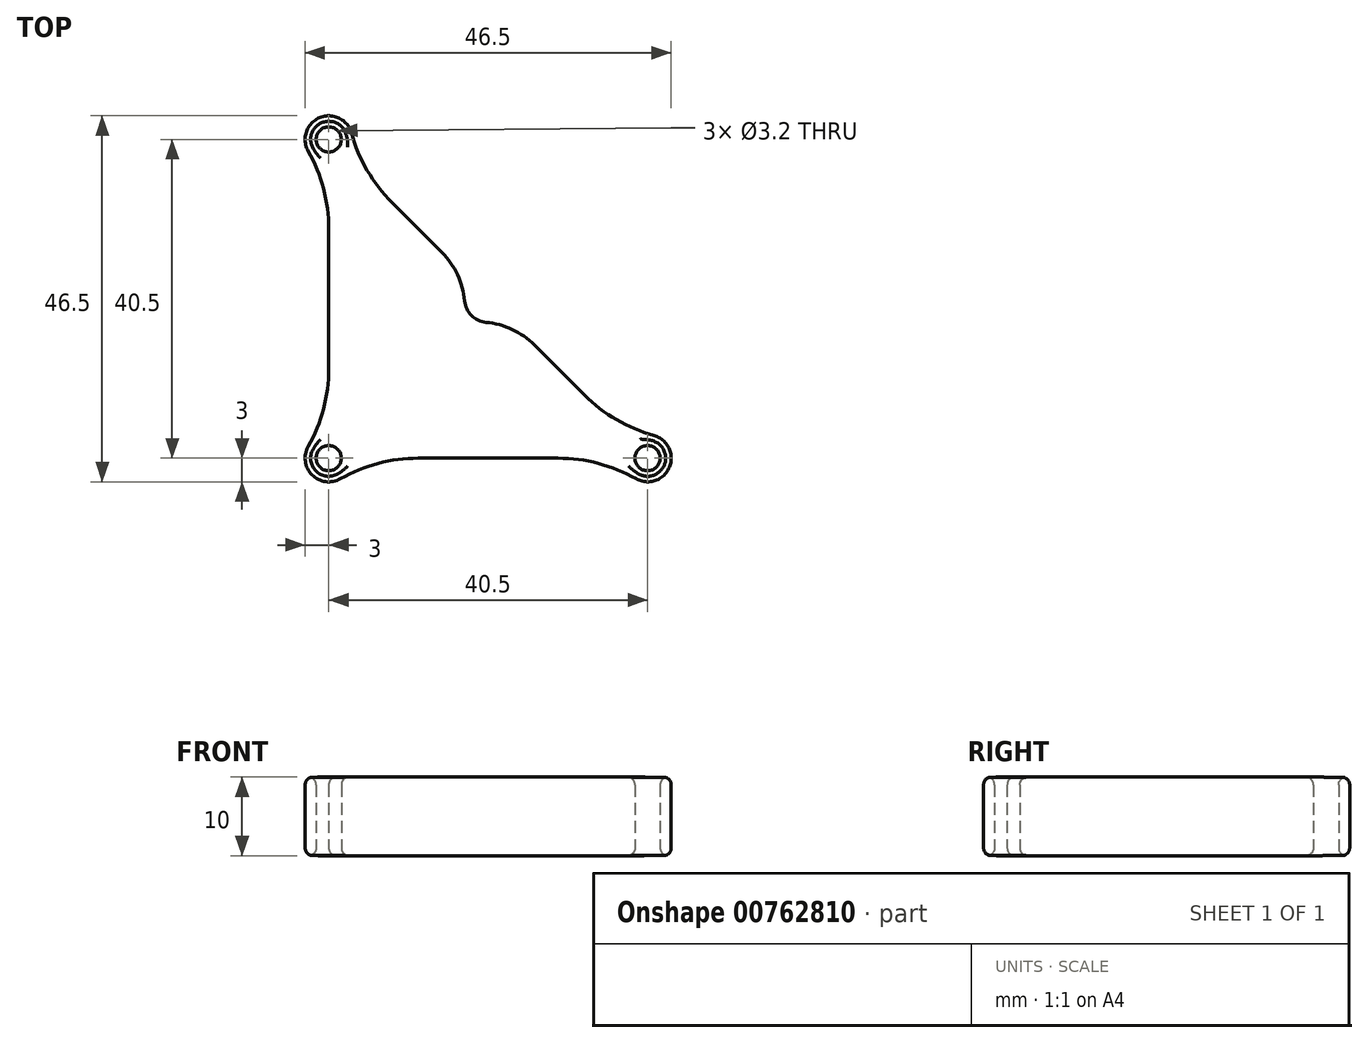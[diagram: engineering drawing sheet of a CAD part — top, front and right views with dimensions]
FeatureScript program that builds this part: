
annotation { "Feature Type Name" : "Feature", "Feature Type Description" : "" }
export const myFeature = defineFeature(function(context is Context, id is Id, definition is map)
    precondition{}
    {
        {
            var Q0;
            Q0=qCreatedBy(makeId("Top.planeOp"),FACE);
            var sketch = newSketch(context, id + "F0", { "sketchPlane" : qUnion([Q0])});
            skLineSegment(sketch, "E0", {"start": v(29.14, 0) * mm, "end": v(11.36, 0) * mm});
            skLineSegment(sketch, "E1", {"start": v(0, 11.36) * mm, "end": v(0, 29.14) * mm});
            skLineSegment(sketch, "E2", {"start": v(8.03, 32.47) * mm, "end": v(14.38, 26.12) * mm});
            skArc(sketch, "E3", {"start": v(17.26, 19.97) * mm, "mid": v(18.13, 18.13) * mm, "end": v(19.97, 17.26) * mm});
            skArc(sketch, "E4", {"start": v(2.9, 41.3) * mm, "mid": v(-1.15, 43.27) * mm, "end": v(-2.6, 39.02) * mm});
            skArc(sketch, "E5", {"start": v(-2.6, 1.48) * mm, "mid": v(-2.12, -2.12) * mm, "end": v(1.48, -2.6) * mm});
            skArc(sketch, "E6", {"start": v(39.02, -2.6) * mm, "mid": v(43.27, -1.15) * mm, "end": v(41.3, 2.9) * mm});
            skLineSegment(sketch, "E7.trimOffspring", {"start": v(26.12, 14.38) * mm, "end": v(32.47, 8.03) * mm});
            skPoint(sketch, "E8.visualSharp", {"position": v(2.12, 38.38) * mm});
            skArc(sketch, "E8.filletArc", {"start": v(2.9, 41.3) * mm, "mid": v(4.89, 36.55) * mm, "end": v(8.03, 32.47) * mm});
            skPoint(sketch, "E9.visualSharp", {"position": v(0, 37.5) * mm});
            skArc(sketch, "E9.filletArc", {"start": v(0, 29.14) * mm, "mid": v(-0.66, 34.25) * mm, "end": v(-2.6, 39.02) * mm});
            skPoint(sketch, "E10.visualSharp", {"position": v(0, 3) * mm});
            skArc(sketch, "E10.filletArc", {"start": v(-2.6, 1.48) * mm, "mid": v(-0.66, 6.25) * mm, "end": v(0, 11.36) * mm});
            skPoint(sketch, "E11.visualSharp", {"position": v(3, 0) * mm});
            skArc(sketch, "E11.filletArc", {"start": v(11.36, 0) * mm, "mid": v(6.25, -0.66) * mm, "end": v(1.48, -2.6) * mm});
            skPoint(sketch, "E12.visualSharp", {"position": v(37.5, 0) * mm});
            skArc(sketch, "E12.filletArc", {"start": v(39.02, -2.6) * mm, "mid": v(34.25, -0.66) * mm, "end": v(29.14, 0) * mm});
            skPoint(sketch, "E13.visualSharp", {"position": v(38.38, 2.12) * mm});
            skArc(sketch, "E13.filletArc", {"start": v(32.47, 8.03) * mm, "mid": v(36.55, 4.89) * mm, "end": v(41.3, 2.9) * mm});
            skPoint(sketch, "E14.visualSharp", {"position": v(18.13, 22.37) * mm});
            skArc(sketch, "E14.filletArc", {"start": v(17.26, 19.97) * mm, "mid": v(16.36, 23.3) * mm, "end": v(14.38, 26.12) * mm});
            skPoint(sketch, "E15.visualSharp", {"position": v(22.37, 18.13) * mm});
            skArc(sketch, "E15.filletArc", {"start": v(26.12, 14.38) * mm, "mid": v(23.3, 16.36) * mm, "end": v(19.97, 17.26) * mm});
            skCircle(sketch, "E16", {"center": v(0, 40.5) * mm, "radius": 1.6 * mm});
            skCircle(sketch, "E17", {"center": v(0, 0) * mm, "radius": 1.6 * mm});
            skCircle(sketch, "E18", {"center": v(40.5, 0) * mm, "radius": 1.6 * mm});
            skSolve(sketch);
        }
        {
            var Q0;
            Q0=makeQuery(id+"F0.imprint","IMPRINT",FACE,{"disambiguationData":[TD([[makeQuery(id+"F0.imprint","IMPRINT",EDGE,{"derivedFrom":sQuery(id+"F0.wireOp",EDGE,"E0")}),-1.0]])]});
            extrude(context, id + "F1", {"entities" : qUnion([Q0]), "depth" : 10 * mm, "offsetDistance" : 25 * mm});
        }
        {
            var Q0;
            Q0=makeQuery(id+"F1.opExtrude","CAP_FACE",FACE,{"disambiguationData":[OSD([sQuery(id+"F0.wireOp",EDGE,"E0"),sQuery(id+"F0.wireOp",EDGE,"E1"),sQuery(id+"F0.wireOp",EDGE,"E2"),sQuery(id+"F0.wireOp",EDGE,"E3"),sQuery(id+"F0.wireOp",EDGE,"E4"),sQuery(id+"F0.wireOp",EDGE,"E5"),sQuery(id+"F0.wireOp",EDGE,"E6"),sQuery(id+"F0.wireOp",EDGE,"E7.trimOffspring"),sQuery(id+"F0.wireOp",EDGE,"E8.filletArc"),sQuery(id+"F0.wireOp",EDGE,"E9.filletArc"),sQuery(id+"F0.wireOp",EDGE,"E10.filletArc"),sQuery(id+"F0.wireOp",EDGE,"E11.filletArc"),sQuery(id+"F0.wireOp",EDGE,"E12.filletArc"),sQuery(id+"F0.wireOp",EDGE,"E13.filletArc"),sQuery(id+"F0.wireOp",EDGE,"E14.filletArc"),sQuery(id+"F0.wireOp",EDGE,"E15.filletArc"),sQuery(id+"F0.wireOp",EDGE,"E16"),sQuery(id+"F0.wireOp",EDGE,"E17"),sQuery(id+"F0.wireOp",EDGE,"E18")])],"isStart":false});
            var Q1;
            Q1=makeQuery(id+"F1.opExtrude","CAP_FACE",FACE,{"disambiguationData":[OSD([sQuery(id+"F0.wireOp",EDGE,"E0"),sQuery(id+"F0.wireOp",EDGE,"E1"),sQuery(id+"F0.wireOp",EDGE,"E2"),sQuery(id+"F0.wireOp",EDGE,"E3"),sQuery(id+"F0.wireOp",EDGE,"E4"),sQuery(id+"F0.wireOp",EDGE,"E5"),sQuery(id+"F0.wireOp",EDGE,"E6"),sQuery(id+"F0.wireOp",EDGE,"E7.trimOffspring"),sQuery(id+"F0.wireOp",EDGE,"E8.filletArc"),sQuery(id+"F0.wireOp",EDGE,"E9.filletArc"),sQuery(id+"F0.wireOp",EDGE,"E10.filletArc"),sQuery(id+"F0.wireOp",EDGE,"E11.filletArc"),sQuery(id+"F0.wireOp",EDGE,"E12.filletArc"),sQuery(id+"F0.wireOp",EDGE,"E13.filletArc"),sQuery(id+"F0.wireOp",EDGE,"E14.filletArc"),sQuery(id+"F0.wireOp",EDGE,"E15.filletArc"),sQuery(id+"F0.wireOp",EDGE,"E16"),sQuery(id+"F0.wireOp",EDGE,"E17"),sQuery(id+"F0.wireOp",EDGE,"E18")])],"isStart":true});
            fillet(context, id + "F2", {"entities" : qUnion([Q0, Q1]), "radius" : 1 * mm, "tangentPropagation" : true, "allowEdgeOverflow" : false});
        }
    });
